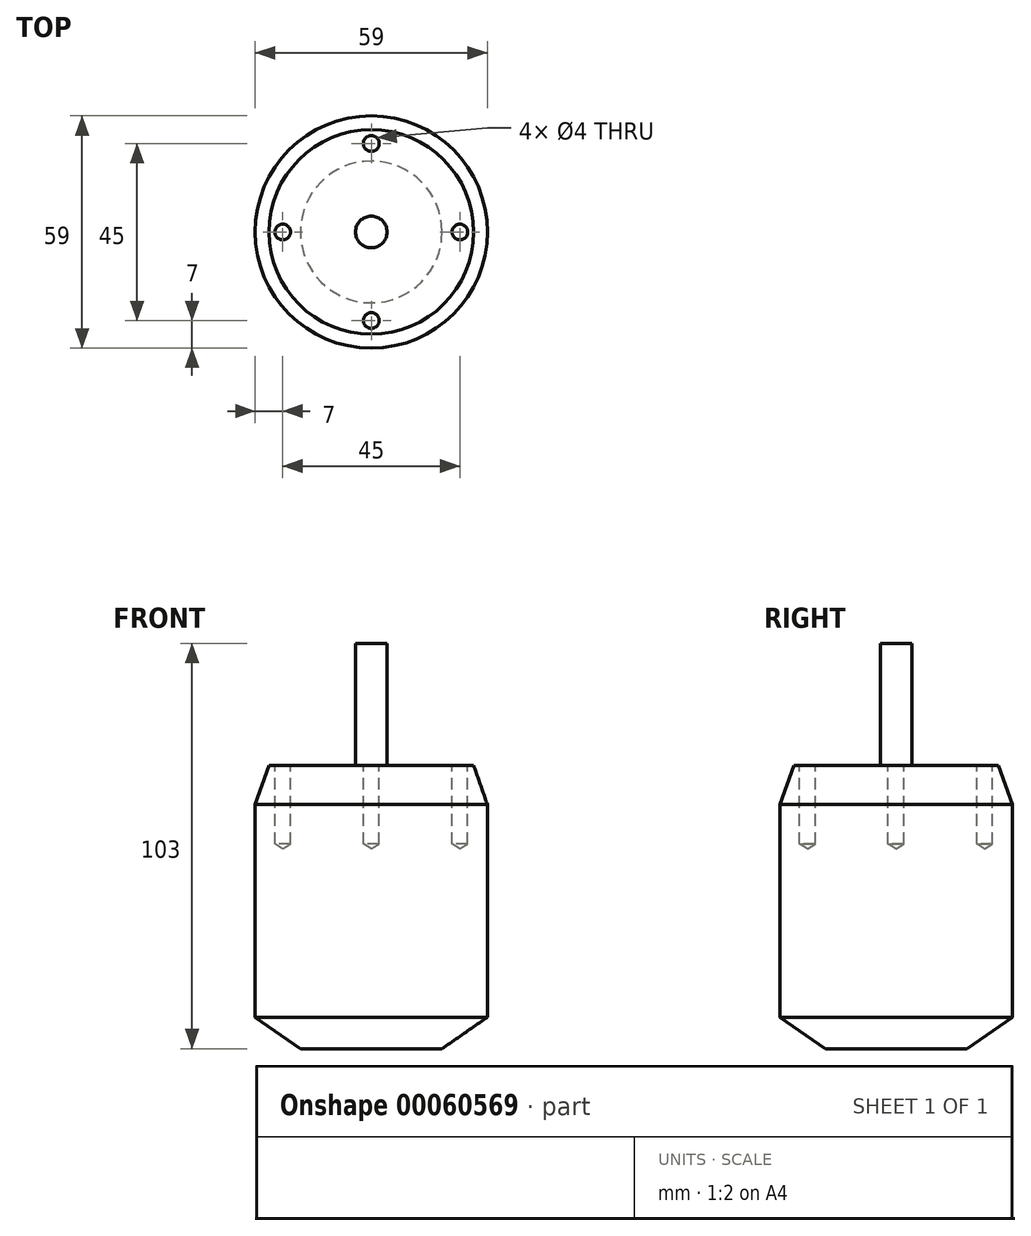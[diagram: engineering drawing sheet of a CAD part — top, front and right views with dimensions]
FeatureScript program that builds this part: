
annotation { "Feature Type Name" : "Feature", "Feature Type Description" : "" }
export const myFeature = defineFeature(function(context is Context, id is Id, definition is map)
    precondition{}
    {
        {
            var Q0;
            Q0=qCreatedBy(makeId("Top.planeOp"),FACE);
            var sketch = newSketch(context, id + "F0", { "sketchPlane" : qUnion([Q0])});
            skCircle(sketch, "E0", {"center": v(0, 0) * mm, "radius": 29.5 * mm});
            skSolve(sketch);
        }
        {
            var Q0;
            Q0 = qSketchRegion(id + "F0", true);
            extrude(context, id + "F1", {"entities" : qUnion([Q0]), "depth" : 72 * mm});
        }
        {
            var Q0;
            Q0=makeQuery(id+"F1.opExtrude","CAP_FACE",FACE,{"disambiguationData":[OSD([sQuery(id+"F0.wireOp",EDGE,"E0")])],"isStart":false});
            chamfer(context, id + "F2", {"entities" : qUnion([Q0]), "chamferType" : ChamferType.TWO_OFFSETS, "width1" : 3.5 * mm, "oppositeDirection" : false, "width2" : 10 * mm, "tangentPropagation" : true});
        }
        {
            var Q0;
            Q0=makeQuery(id+"F1.opExtrude","CAP_FACE",FACE,{"disambiguationData":[OSD([sQuery(id+"F0.wireOp",EDGE,"E0")])],"isStart":true});
            chamfer(context, id + "F3", {"entities" : qUnion([Q0]), "chamferType" : ChamferType.TWO_OFFSETS, "width1" : 8 * mm, "oppositeDirection" : false, "width2" : 11.5 * mm, "tangentPropagation" : true});
        }
        {
            var Q0;
            Q0=qCreatedBy(makeId("Top.planeOp"),FACE);
            var sketch = newSketch(context, id + "F4", { "sketchPlane" : qUnion([Q0])});
            skCircle(sketch, "E1", {"center": v(0, 0) * mm, "radius": 4 * mm});
            skSolve(sketch);
        }
        {
            var Q0;
            Q0=makeQuery(id+"F4.imprint","IMPRINT",FACE,{"disambiguationData":[TD([[makeQuery(id+"F4.imprint","IMPRINT",EDGE,{"derivedFrom":sQuery(id+"F4.wireOp",EDGE,"E1")}),1.0]])]});
            extrude(context, id + "F5", {"entities" : qUnion([Q0]), "operationType" : NewBodyOperationType.ADD, "depth" : 103 * mm});
        }
        {
            var Q0;
            Q0=makeQuery(id+"F1.opExtrude","CAP_FACE",FACE,{"disambiguationData":[OSD([sQuery(id+"F0.wireOp",EDGE,"E0")])],"isStart":false});
            var sketch = newSketch(context, id + "F6", { "sketchPlane" : qUnion([Q0])});
            skCircle(sketch, "E2", {"center": v(0, 0) * mm, "radius": 22.5 * mm});
            skPoint(sketch, "E3", {"position": v(0, 22.5) * mm});
            skPoint(sketch, "E4", {"position": v(22.5, 0) * mm});
            skPoint(sketch, "E5", {"position": v(0, -22.5) * mm});
            skPoint(sketch, "E6", {"position": v(-22.5, 0) * mm});
            skSolve(sketch);
        }
        {
            var Q0;
            Q0=sQuery(id+"F6.wireOp",VERTEX,"E3");
            var Q1;
            Q1=sQuery(id+"F6.wireOp",VERTEX,"E4");
            var Q2;
            Q2=sQuery(id+"F6.wireOp",VERTEX,"E5");
            var Q3;
            Q3=sQuery(id+"F6.wireOp",VERTEX,"E6");
            var Q4;
            Q4=makeQuery(id+"F1.opExtrude","SWEPT_BODY",BODY,{"disambiguationData":[OSD([sQuery(id+"F0.wireOp",EDGE,"E0")])]});
            hole(context, id + "F7", {"style" : HoleStyle.SIMPLE, "holeDiameter" : 4 * mm, "endStyle" : HoleEndStyle.BLIND, "holeDepth" : 20 * mm, "locations" : qUnion([Q0, Q1, Q2, Q3]), "scope" : qUnion([Q4])});
        }
    });
